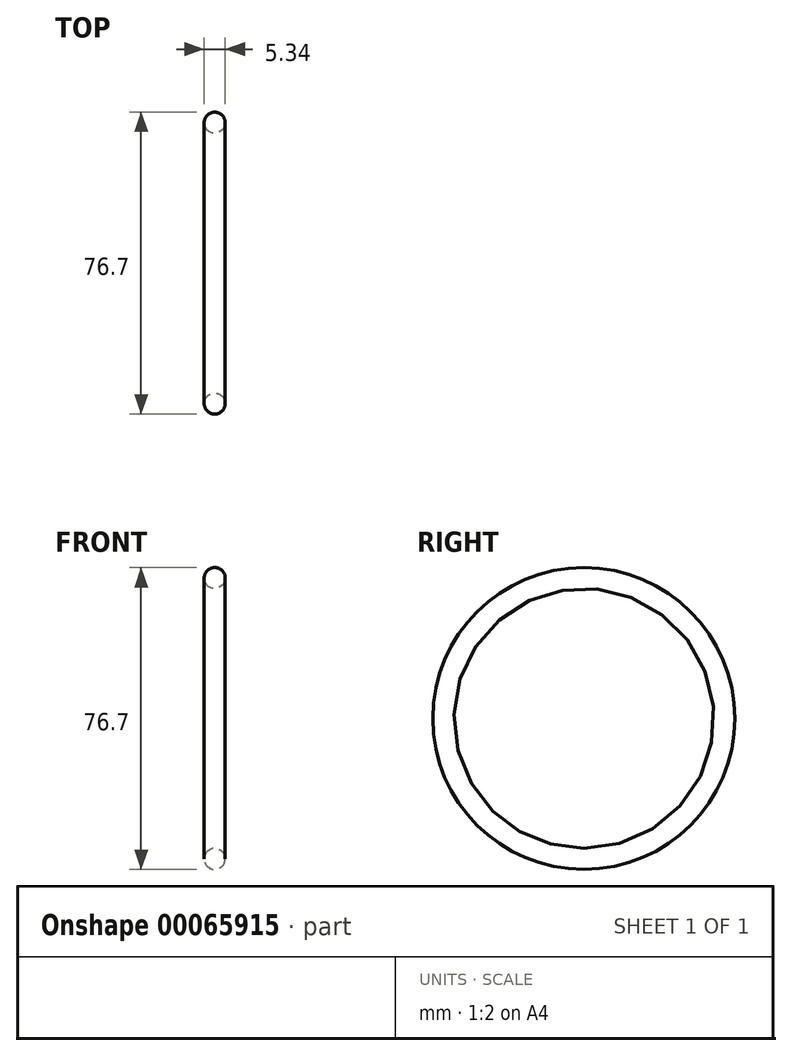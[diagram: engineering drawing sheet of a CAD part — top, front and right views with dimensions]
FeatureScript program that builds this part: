
annotation { "Feature Type Name" : "Feature", "Feature Type Description" : "" }
export const myFeature = defineFeature(function(context is Context, id is Id, definition is map)
    precondition{}
    {
        {
            var Q0;
            Q0=qCreatedBy(makeId("Front.planeOp"),FACE);
            var sketch = newSketch(context, id + "F0", { "sketchPlane" : qUnion([Q0])});
            skLineSegment(sketch, "E0", {"start": v(0, 0) * mm, "end": v(-6.06, 0) * mm, "construction": true});
            skCircle(sketch, "E1", {"center": v(0, 35.69) * mm, "radius": 2.67 * mm});
            skSolve(sketch);
        }
        {
            var Q0;
            Q0=makeQuery(id+"F0.imprint","IMPRINT",FACE,{"disambiguationData":[TD([[makeQuery(id+"F0.imprint","IMPRINT",EDGE,{"derivedFrom":sQuery(id+"F0.wireOp",EDGE,"E1")}),1.0]])]});
            var Q1;
            Q1=sQuery(id+"F0.wireOp",EDGE,"E0");
            revolve(context, id + "F1", {"entities" : qUnion([Q0]), "axis" : qUnion([Q1]), "revolveType" : RevolveType.FULL});
        }
    });
